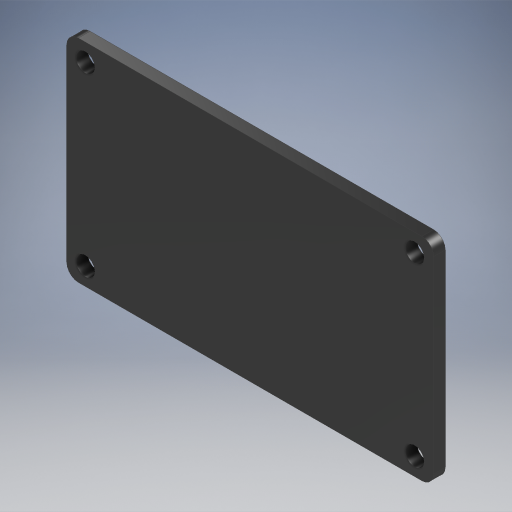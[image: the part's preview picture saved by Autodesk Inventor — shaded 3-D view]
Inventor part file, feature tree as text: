
AUTODESK INVENTOR PART (.ipt)
format: ipt  version: 2024.2 (Build 282272000, 272)  size: 239,616 bytes
history: native  units: in
note: dims shown in document units (in); Inventor stores cm internally (conversion verified against a paired STEP export)
features: extrude x1, fillet x1, sketch x1
ambient origin geometry x8: Origin, YZ Plane, XZ Plane, XY Plane, X Axis, Y Axis, Z Axis, Center Point
bodies: Solid1 (feature_tree)
feature tree (3):
  extrude  "Extrusion1"  Depth=0.125in
  fillet  "Fillet1"  Radius=3.5in
  sketch  "Sketch1"  dims[d0=0.202in d1=0.202in d2=3.5in d3=0.7874in d5=1.875in d6=0.3937in d8=1.0in d10=3.9in d11=2.25in d12=0.125in d13=0.0in d14=0.125in]
